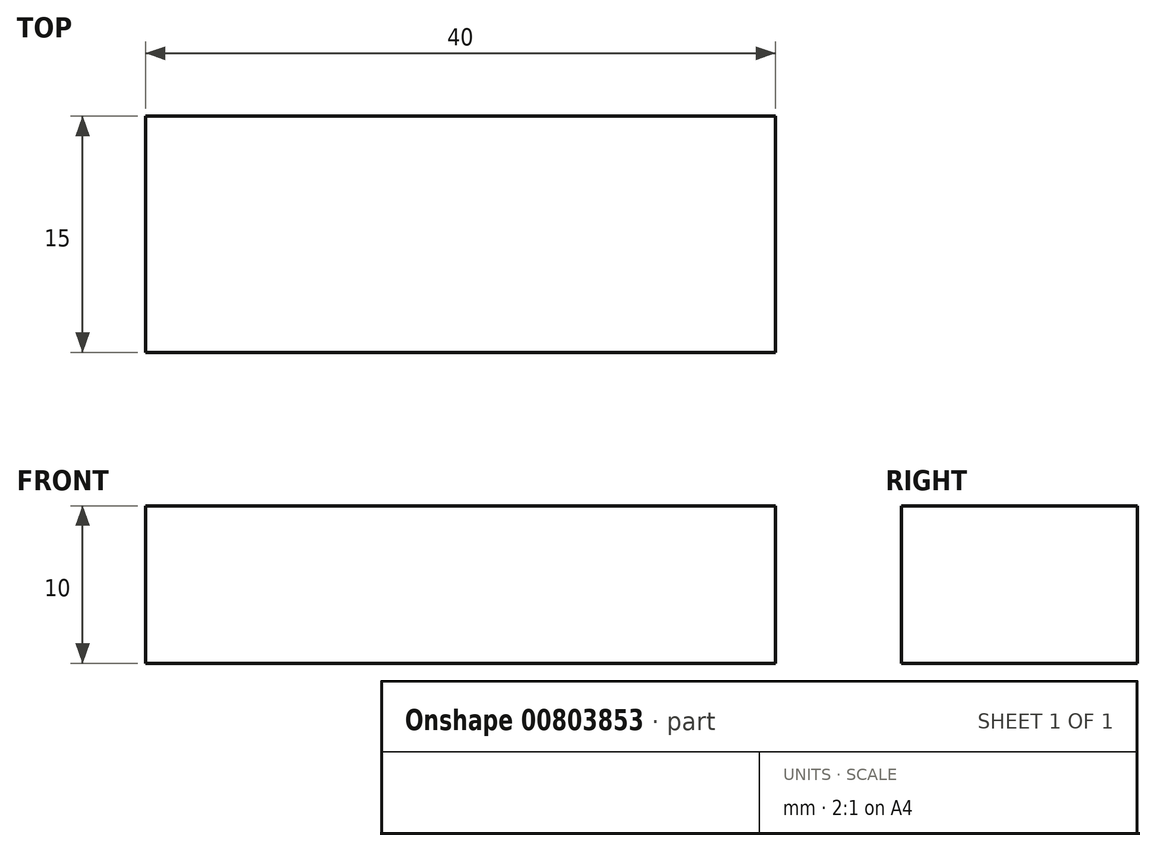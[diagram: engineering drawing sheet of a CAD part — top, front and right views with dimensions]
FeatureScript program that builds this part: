
annotation { "Feature Type Name" : "Feature", "Feature Type Description" : "" }
export const myFeature = defineFeature(function(context is Context, id is Id, definition is map)
    precondition{}
    {
        {
            var Q0;
            Q0=qCreatedBy(makeId("Top.planeOp"),FACE);
            var sketch = newSketch(context, id + "F0", { "sketchPlane" : qUnion([Q0])});
            skLineSegment(sketch, "E0.bottom", {"start": v(0, 15) * mm, "end": v(40, 15) * mm});
            skLineSegment(sketch, "E0.top", {"start": v(0, 0) * mm, "end": v(40, 0) * mm});
            skLineSegment(sketch, "E0.left", {"start": v(0, 15) * mm, "end": v(0, 0) * mm});
            skLineSegment(sketch, "E0.right", {"start": v(40, 15) * mm, "end": v(40, 0) * mm});
            skSolve(sketch);
        }
        {
            var Q0;
            Q0=makeQuery(id+"F0.imprint","IMPRINT",FACE,{"disambiguationData":[TD([[makeQuery(id+"F0.imprint","IMPRINT",EDGE,{"derivedFrom":sQuery(id+"F0.wireOp",EDGE,"E0.bottom")}),-1.0]])]});
            extrude(context, id + "F1", {"entities" : qUnion([Q0]), "depth" : 10 * mm, "offsetDistance" : 25 * mm});
        }
    });
